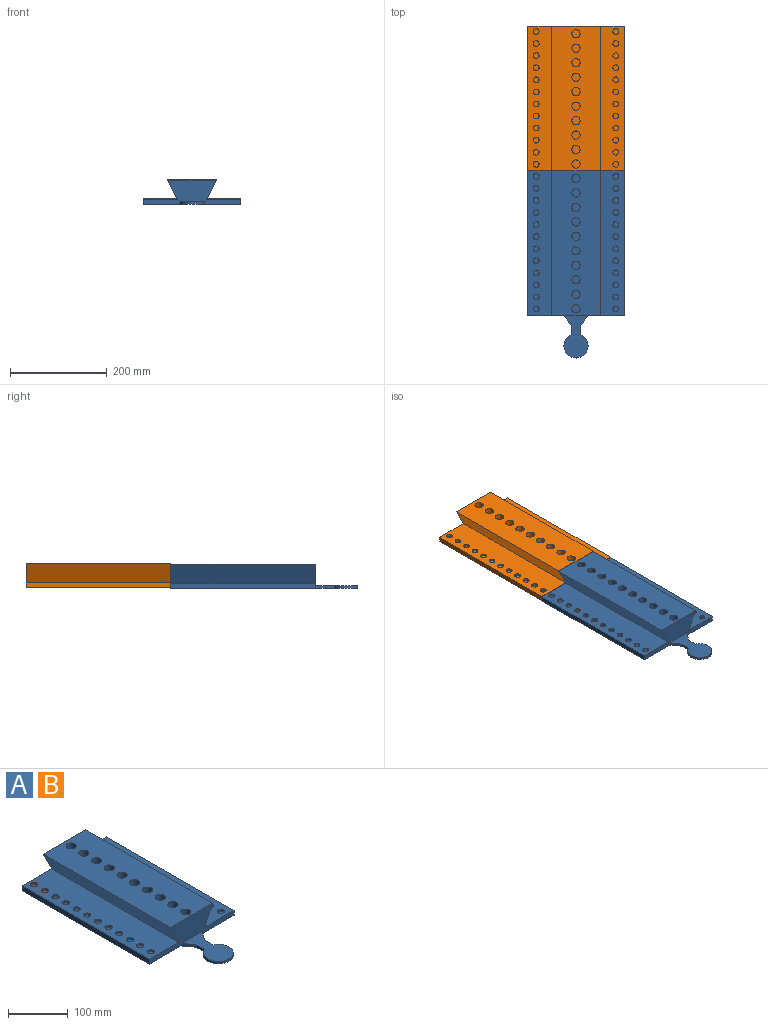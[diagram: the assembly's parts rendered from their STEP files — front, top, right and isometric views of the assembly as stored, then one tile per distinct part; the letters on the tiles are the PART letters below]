
ASSEMBLY  parts=2 mates=1
PART A: 90 faces, bbox 200x387.9x49.8 mm
  f0: plane 387.91x200mm, normal (0,0,-1), area 60002.3mm2, adj f1,f7,f8,f9,f78,f79,f80,f81
  f1: plane 300x10mm, normal (1,0,0), area 3000mm2, adj f0,f2,f8,f9
  f2: plane 300x70mm, normal (0,0,1), area 19642.8mm2, adj f1,f3,f8,f9,f34,f36,f38,f40
  f3: plane 300x39.83mm, normal (0.89,0,-0.45), area 13370.9mm2, adj f2,f4,f8,f9
  f4: plane 300x100mm, normal (0,0,1), area 27730.2mm2, adj f3,f5,f8,f9,f58,f60,f62,f64
  f5: plane 300x39.83mm, normal (-0.89,0,-0.45), area 13370.9mm2, adj f4,f6,f8,f9
  f6: plane 300x70mm, normal (0,0,1), area 19642.8mm2, adj f5,f7,f8,f9,f10,f12,f14,f16
  f7: plane 300x10mm, normal (-1,0,0), area 3000mm2, adj f0,f6,f8,f9
  f8: plane 200x49.83mm, normal (0,-1,0), area 4936.4mm2, adj f0,f1,f2,f3,f4,f5,f6,f7
  f9: plane 200x49.83mm, normal (0,1,0), area 4887.1mm2, adj f0,f1,f2,f3,f4,f5,f6,f7
  f10: cylinder r=6mm len=12mm, axis (0,0,1), area 150.8mm2, adj f6,f11
  f11: plane 12x12mm, normal (0,0,1), area 113.1mm2, adj f10
  f12: cylinder r=6mm len=12mm, axis (0,0,1), area 150.8mm2, adj f6,f13
  f13: plane 12x12mm, normal (0,0,1), area 113.1mm2, adj f12
  f14: cylinder r=6mm len=12mm, axis (0,0,1), area 150.8mm2, adj f6,f15
  f15: plane 12x12mm, normal (0,0,1), area 113.1mm2, adj f14
  f16: cylinder r=6mm len=12mm, axis (0,0,1), area 150.8mm2, adj f6,f17
  f17: plane 12x12mm, normal (0,0,1), area 113.1mm2, adj f16
  f18: cylinder r=6mm len=12mm, axis (0,0,1), area 150.8mm2, adj f6,f19
  f19: plane 12x12mm, normal (0,0,1), area 113.1mm2, adj f18
  f20: cylinder r=6mm len=12mm, axis (0,0,1), area 150.8mm2, adj f6,f21
  f21: plane 12x12mm, normal (0,0,1), area 113.1mm2, adj f20
  f22: cylinder r=6mm len=12mm, axis (0,0,1), area 150.8mm2, adj f6,f23
  f23: plane 12x12mm, normal (0,0,1), area 113.1mm2, adj f22
  f24: cylinder r=6mm len=12mm, axis (0,0,1), area 150.8mm2, adj f6,f25
  f25: plane 12x12mm, normal (0,0,1), area 113.1mm2, adj f24
  f26: cylinder r=6mm len=12mm, axis (0,0,1), area 150.8mm2, adj f6,f27
  f27: plane 12x12mm, normal (0,0,1), area 113.1mm2, adj f26
  f28: cylinder r=6mm len=12mm, axis (0,0,1), area 150.8mm2, adj f6,f29
  f29: plane 12x12mm, normal (0,0,1), area 113.1mm2, adj f28
  f30: cylinder r=6mm len=12mm, axis (0,0,1), area 150.8mm2, adj f6,f31
  f31: plane 12x12mm, normal (0,0,1), area 113.1mm2, adj f30
  f32: cylinder r=6mm len=12mm, axis (0,0,1), area 150.8mm2, adj f6,f33
  f33: plane 12x12mm, normal (0,0,1), area 113.1mm2, adj f32
  f34: cylinder r=6mm len=12mm, axis (0,0,1), area 150.8mm2, adj f2,f35
  f35: plane 12x12mm, normal (0,0,1), area 113.1mm2, adj f34
  f36: cylinder r=6mm len=12mm, axis (0,0,1), area 150.8mm2, adj f2,f37
  f37: plane 12x12mm, normal (0,0,1), area 113.1mm2, adj f36
  f38: cylinder r=6mm len=12mm, axis (0,0,1), area 150.8mm2, adj f2,f39
  f39: plane 12x12mm, normal (0,0,1), area 113.1mm2, adj f38
  f40: cylinder r=6mm len=12mm, axis (0,0,1), area 150.8mm2, adj f2,f41
  f41: plane 12x12mm, normal (0,0,1), area 113.1mm2, adj f40
  f42: cylinder r=6mm len=12mm, axis (0,0,1), area 150.8mm2, adj f2,f43
  f43: plane 12x12mm, normal (0,0,1), area 113.1mm2, adj f42
  f44: cylinder r=6mm len=12mm, axis (0,0,1), area 150.8mm2, adj f2,f45
  f45: plane 12x12mm, normal (0,0,1), area 113.1mm2, adj f44
  f46: cylinder r=6mm len=12mm, axis (0,0,1), area 150.8mm2, adj f2,f47
  f47: plane 12x12mm, normal (0,0,1), area 113.1mm2, adj f46
  f48: cylinder r=6mm len=12mm, axis (0,0,1), area 150.8mm2, adj f2,f49
  f49: plane 12x12mm, normal (0,0,1), area 113.1mm2, adj f48
  f50: cylinder r=6mm len=12mm, axis (0,0,1), area 150.8mm2, adj f2,f51
  f51: plane 12x12mm, normal (0,0,1), area 113.1mm2, adj f50
  f52: cylinder r=6mm len=12mm, axis (0,0,1), area 150.8mm2, adj f2,f53
  f53: plane 12x12mm, normal (0,0,1), area 113.1mm2, adj f52
  f54: cylinder r=6mm len=12mm, axis (0,0,1), area 150.8mm2, adj f2,f55
  f55: plane 12x12mm, normal (0,0,1), area 113.1mm2, adj f54
  f56: cylinder r=6mm len=12mm, axis (0,0,1), area 150.8mm2, adj f2,f57
  f57: plane 12x12mm, normal (0,0,1), area 113.1mm2, adj f56
  f58: cylinder r=8.5mm len=30mm, axis (0,0,1), area 1602.2mm2, adj f4,f59
  f59: plane 17x17mm, normal (0,0,1), area 227mm2, adj f58
  f60: cylinder r=8.5mm len=30mm, axis (0,0,1), area 1602.2mm2, adj f4,f61
  f61: plane 17x17mm, normal (0,0,1), area 227mm2, adj f60
  f62: cylinder r=8.5mm len=30mm, axis (0,0,1), area 1602.2mm2, adj f4,f63
  f63: plane 17x17mm, normal (0,0,1), area 227mm2, adj f62
  f64: cylinder r=8.5mm len=30mm, axis (0,0,1), area 1602.2mm2, adj f4,f65
  f65: plane 17x17mm, normal (0,0,1), area 227mm2, adj f64
  f66: cylinder r=8.5mm len=30mm, axis (0,0,1), area 1602.2mm2, adj f4,f67
  f67: plane 17x17mm, normal (0,0,1), area 227mm2, adj f66
  f68: cylinder r=8.5mm len=30mm, axis (0,0,1), area 1602.2mm2, adj f4,f69
  f69: plane 17x17mm, normal (0,0,1), area 227mm2, adj f68
  f70: cylinder r=8.5mm len=30mm, axis (0,0,1), area 1602.2mm2, adj f4,f71
  f71: plane 17x17mm, normal (0,0,1), area 227mm2, adj f70
  f72: cylinder r=8.5mm len=30mm, axis (0,0,1), area 1602.2mm2, adj f4,f73
  f73: plane 17x17mm, normal (0,0,1), area 227mm2, adj f72
  f74: cylinder r=8.5mm len=30mm, axis (0,0,1), area 1602.2mm2, adj f4,f75
  f75: plane 17x17mm, normal (0,0,1), area 227mm2, adj f74
  f76: cylinder r=8.5mm len=30mm, axis (0,0,1), area 1602.2mm2, adj f4,f77
  f77: plane 17x17mm, normal (0,0,1), area 227mm2, adj f76
  f78: plane 20x5mm, normal (-1,0,0), area 100mm2, adj f0,f79,f82,f83
  f79: plane 20x15mm, normal (-0.8,-0.6,0), area 125mm2, adj f0,f8,f78,f83
  f80: plane 20x15mm, normal (0.8,-0.6,0), area 125mm2, adj f0,f8,f81,f83
  f81: plane 20x5mm, normal (1,0,0), area 100mm2, adj f0,f80,f82,f83
  f82: cylinder r=25mm len=50mm, axis (0,0,-1), area 682.5mm2, adj f0,f78,f81,f83
  f83: plane 87.91x50mm, normal (0,0,1), area 3035.4mm2, adj f8,f78,f79,f80,f81,f82
  f84: plane 20x6mm, normal (1,0,0), area 120mm2, adj f0,f85,f88,f89
  f85: plane 20x15mm, normal (0.8,0.6,0), area 150mm2, adj f0,f9,f84,f89
  f86: plane 19.84x14.88mm, normal (-0.8,0.6,0), area 148.8mm2, adj f0,f9,f87,f89
  f87: plane 20.16x6mm, normal (-1,0,0), area 120.9mm2, adj f0,f86,f88,f89
  f88: cylinder r=25mm len=50mm, axis (0,0,-1), area 819mm2, adj f0,f84,f87,f89
  f89: plane 87.91x50mm, normal (0,0,-1), area 3033.1mm2, adj f9,f84,f85,f86,f87,f88
PART B: same geometry as A
PLACE A at identity
PLACE B t=(0,300,1)mm
MATE fastened B.f82 <-> A.f88  axis (0,0,1) through (-10.59,-62.91,6)mm
